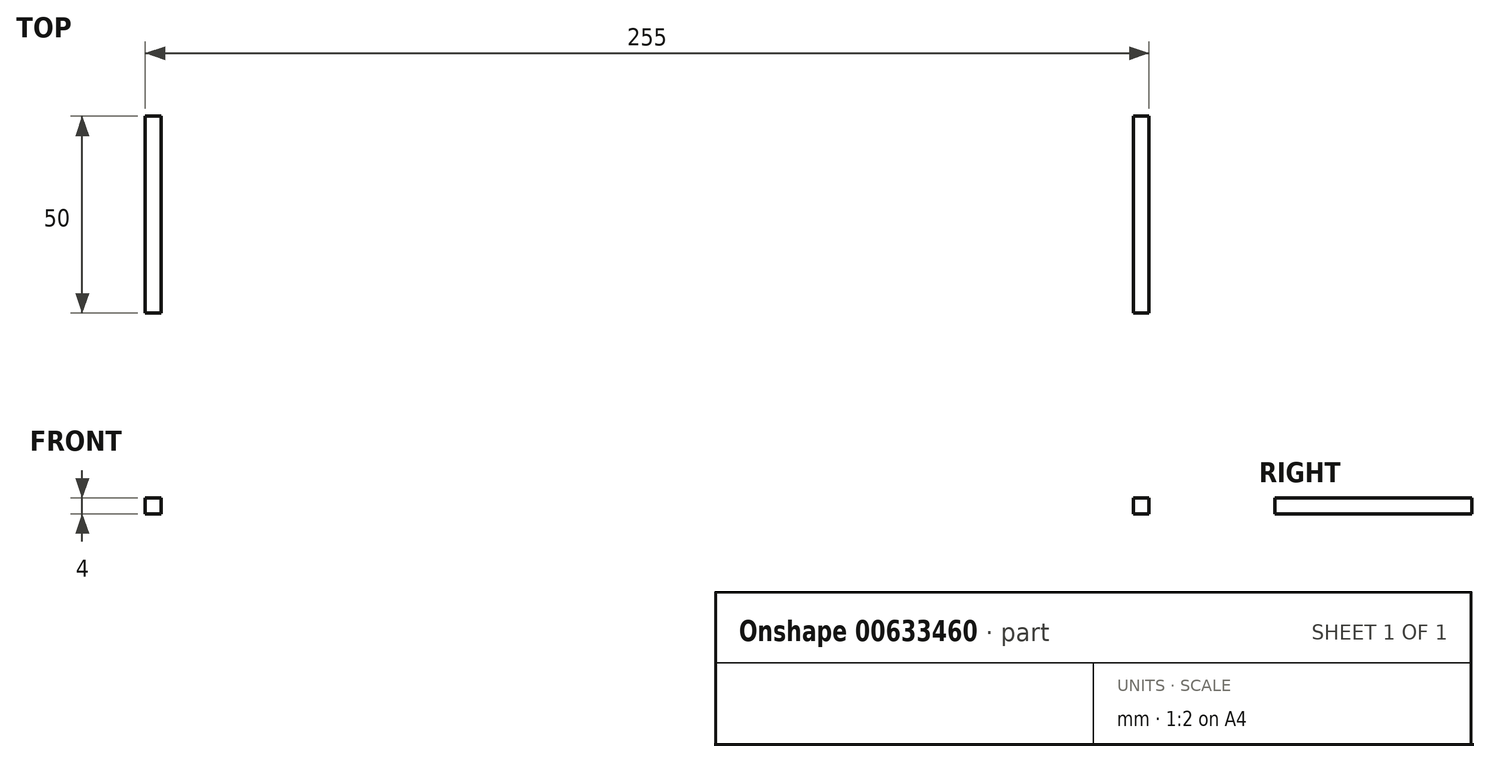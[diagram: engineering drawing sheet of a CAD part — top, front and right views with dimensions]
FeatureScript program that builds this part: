
annotation { "Feature Type Name" : "Feature", "Feature Type Description" : "" }
export const myFeature = defineFeature(function(context is Context, id is Id, definition is map)
    precondition{}
    {
        {
            var Q0;
            Q0=qCreatedBy(makeId("Top.planeOp"),FACE);
            var sketch = newSketch(context, id + "F0", { "sketchPlane" : qUnion([Q0])});
            skLineSegment(sketch, "E0.bottom", {"start": v(0, 0) * mm, "end": v(-255, 0) * mm});
            skLineSegment(sketch, "E0.top", {"start": v(0, 300) * mm, "end": v(-255, 300) * mm});
            skLineSegment(sketch, "E0.left", {"start": v(0, 0) * mm, "end": v(0, 300) * mm});
            skLineSegment(sketch, "E0.right", {"start": v(-255, 0) * mm, "end": v(-255, 300) * mm});
            skLineSegment(sketch, "E1.bottom", {"start": v(-27, 0) * mm, "end": v(-227, 0) * mm});
            skLineSegment(sketch, "E1.top", {"start": v(-27, 220) * mm, "end": v(-227, 220) * mm});
            skLineSegment(sketch, "E1.left", {"start": v(-27, 0) * mm, "end": v(-27, 220) * mm});
            skLineSegment(sketch, "E1.right", {"start": v(-227, 0) * mm, "end": v(-227, 220) * mm});
            skLineSegment(sketch, "E2.bottom", {"start": v(-255, 300) * mm, "end": v(-251, 300) * mm});
            skLineSegment(sketch, "E2.top", {"start": v(-255, 250) * mm, "end": v(-251, 250) * mm});
            skLineSegment(sketch, "E2.left", {"start": v(-255, 300) * mm, "end": v(-255, 250) * mm});
            skLineSegment(sketch, "E2.right", {"start": v(-251, 300) * mm, "end": v(-251, 250) * mm});
            skLineSegment(sketch, "E3.bottom", {"start": v(-255, 200) * mm, "end": v(-251, 200) * mm});
            skLineSegment(sketch, "E3.top", {"start": v(-255, 150) * mm, "end": v(-251, 150) * mm});
            skLineSegment(sketch, "E3.left", {"start": v(-255, 200) * mm, "end": v(-255, 150) * mm});
            skLineSegment(sketch, "E3.right", {"start": v(-251, 200) * mm, "end": v(-251, 150) * mm});
            skLineSegment(sketch, "E4.bottom", {"start": v(-255, 0) * mm, "end": v(-251, 0) * mm});
            skLineSegment(sketch, "E4.top", {"start": v(-255, 19.56) * mm, "end": v(-251, 19.56) * mm});
            skLineSegment(sketch, "E4.left", {"start": v(-255, 0) * mm, "end": v(-255, 19.56) * mm});
            skLineSegment(sketch, "E4.right", {"start": v(-251, 0) * mm, "end": v(-251, 19.56) * mm});
            skLineSegment(sketch, "E5.bottom", {"start": v(-255, 100) * mm, "end": v(-251, 100) * mm});
            skLineSegment(sketch, "E5.top", {"start": v(-255, 50) * mm, "end": v(-251, 50) * mm});
            skLineSegment(sketch, "E5.left", {"start": v(-255, 100) * mm, "end": v(-255, 50) * mm});
            skLineSegment(sketch, "E5.right", {"start": v(-251, 100) * mm, "end": v(-251, 50) * mm});
            skLineSegment(sketch, "E6.bottom", {"start": v(0, 300) * mm, "end": v(-4, 300) * mm});
            skLineSegment(sketch, "E6.top", {"start": v(0, 250) * mm, "end": v(-4, 250) * mm});
            skLineSegment(sketch, "E6.left", {"start": v(0, 300) * mm, "end": v(0, 250) * mm});
            skLineSegment(sketch, "E6.right", {"start": v(-4, 300) * mm, "end": v(-4, 250) * mm});
            skLineSegment(sketch, "E7.bottom", {"start": v(0, 200) * mm, "end": v(-4, 200) * mm});
            skLineSegment(sketch, "E7.top", {"start": v(0, 150) * mm, "end": v(-4, 150) * mm});
            skLineSegment(sketch, "E7.left", {"start": v(0, 200) * mm, "end": v(0, 150) * mm});
            skLineSegment(sketch, "E7.right", {"start": v(-4, 200) * mm, "end": v(-4, 150) * mm});
            skLineSegment(sketch, "E8.bottom", {"start": v(0, 100) * mm, "end": v(-4, 100) * mm});
            skLineSegment(sketch, "E8.top", {"start": v(0, 50) * mm, "end": v(-4, 50) * mm});
            skLineSegment(sketch, "E8.left", {"start": v(0, 100) * mm, "end": v(0, 50) * mm});
            skLineSegment(sketch, "E8.right", {"start": v(-4, 100) * mm, "end": v(-4, 50) * mm});
            skLineSegment(sketch, "E9.bottom", {"start": v(0, 19.56) * mm, "end": v(-4, 19.56) * mm});
            skLineSegment(sketch, "E9.top", {"start": v(0, 0) * mm, "end": v(-4, 0) * mm});
            skLineSegment(sketch, "E9.left", {"start": v(0, 19.56) * mm, "end": v(0, 0) * mm});
            skLineSegment(sketch, "E9.right", {"start": v(-4, 19.56) * mm, "end": v(-4, 0) * mm});
            skLineSegment(sketch, "E10.bottom", {"start": v(-27, 220) * mm, "end": v(-23, 220) * mm});
            skLineSegment(sketch, "E10.top", {"start": v(-27, 210) * mm, "end": v(-23, 210) * mm});
            skLineSegment(sketch, "E10.left", {"start": v(-27, 220) * mm, "end": v(-27, 210) * mm});
            skLineSegment(sketch, "E10.right", {"start": v(-23, 220) * mm, "end": v(-23, 210) * mm});
            skLineSegment(sketch, "E11.bottom", {"start": v(-27, 200) * mm, "end": v(-23, 200) * mm});
            skLineSegment(sketch, "E11.top", {"start": v(-27, 190) * mm, "end": v(-23, 190) * mm});
            skLineSegment(sketch, "E11.left", {"start": v(-27, 200) * mm, "end": v(-27, 190) * mm});
            skLineSegment(sketch, "E11.right", {"start": v(-23, 200) * mm, "end": v(-23, 190) * mm});
            skLineSegment(sketch, "E12.bottom", {"start": v(-27, 180) * mm, "end": v(-23, 180) * mm});
            skLineSegment(sketch, "E12.top", {"start": v(-27, 170) * mm, "end": v(-23, 170) * mm});
            skLineSegment(sketch, "E12.left", {"start": v(-27, 180) * mm, "end": v(-27, 170) * mm});
            skLineSegment(sketch, "E12.right", {"start": v(-23, 180) * mm, "end": v(-23, 170) * mm});
            skLineSegment(sketch, "E13.bottom", {"start": v(-227, 220) * mm, "end": v(-231, 220) * mm});
            skLineSegment(sketch, "E13.top", {"start": v(-227, 210) * mm, "end": v(-231, 210) * mm});
            skLineSegment(sketch, "E13.left", {"start": v(-227, 220) * mm, "end": v(-227, 210) * mm});
            skLineSegment(sketch, "E13.right", {"start": v(-231, 220) * mm, "end": v(-231, 210) * mm});
            skLineSegment(sketch, "E14.bottom", {"start": v(-227, 180) * mm, "end": v(-231, 180) * mm});
            skLineSegment(sketch, "E14.top", {"start": v(-227, 170) * mm, "end": v(-231, 170) * mm});
            skLineSegment(sketch, "E14.left", {"start": v(-227, 180) * mm, "end": v(-227, 170) * mm});
            skLineSegment(sketch, "E14.right", {"start": v(-231, 180) * mm, "end": v(-231, 170) * mm});
            skLineSegment(sketch, "E15.bottom", {"start": v(-227, 200) * mm, "end": v(-231, 200) * mm});
            skLineSegment(sketch, "E15.top", {"start": v(-227, 190) * mm, "end": v(-231, 190) * mm});
            skLineSegment(sketch, "E15.left", {"start": v(-227, 200) * mm, "end": v(-227, 190) * mm});
            skLineSegment(sketch, "E15.right", {"start": v(-231, 200) * mm, "end": v(-231, 190) * mm});
            skSolve(sketch);
        }
        {
            var Q0;
            Q0=makeQuery(id+"F0.imprint","IMPRINT",FACE,{"disambiguationData":[TD([[makeQuery(id+"F0.imprint","IMPRINT",EDGE,{"derivedFrom":sQuery(id+"F0.wireOp",EDGE,"E0.top")}),1.0]])]});
            extrude(context, id + "F1", {"entities" : qUnion([Q0]), "depth" : 4 * mm, "offsetDistance" : 25 * mm});
        }
    });
